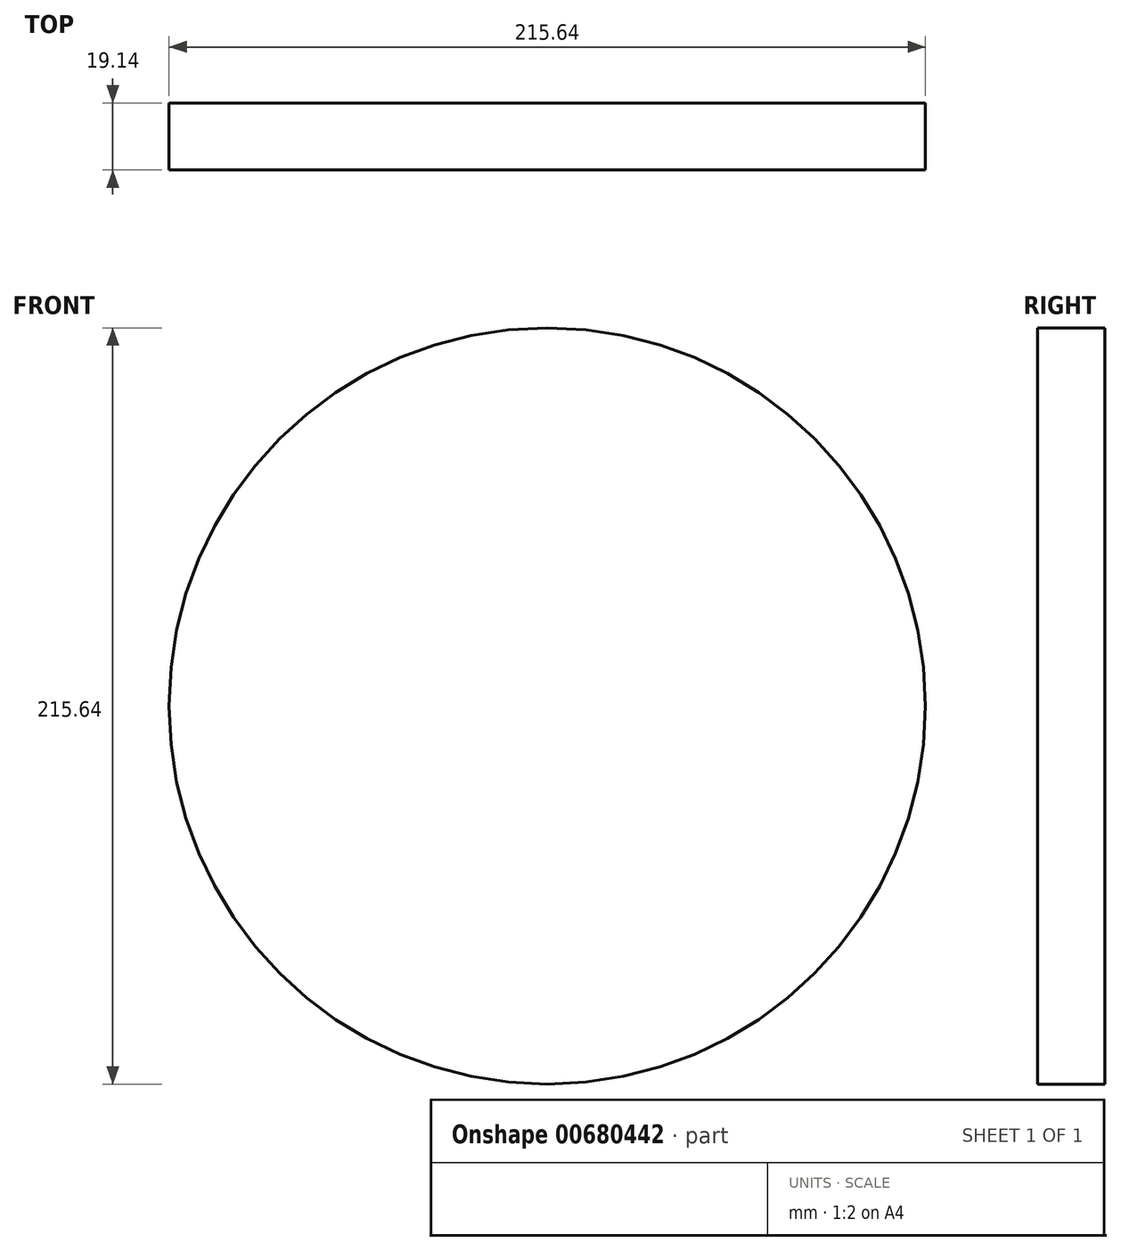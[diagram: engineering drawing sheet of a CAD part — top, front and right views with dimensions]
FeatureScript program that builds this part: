
annotation { "Feature Type Name" : "Feature", "Feature Type Description" : "" }
export const myFeature = defineFeature(function(context is Context, id is Id, definition is map)
    precondition{}
    {
        {
            var Q0;
            Q0=qCreatedBy(makeId("Front.planeOp"),FACE);
            var sketch = newSketch(context, id + "F0", { "sketchPlane" : qUnion([Q0])});
            skCircle(sketch, "E0", {"center": v(0, 0) * mm, "radius": 107.82 * mm});
            skSolve(sketch);
        }
        {
            var Q0;
            Q0=makeQuery(id+"F0.imprint","IMPRINT",FACE,{"disambiguationData":[TD([[makeQuery(id+"F0.imprint","IMPRINT",EDGE,{"derivedFrom":sQuery(id+"F0.wireOp",EDGE,"E0")}),1.0]])]});
            extrude(context, id + "F1", {"entities" : qUnion([Q0]), "depth" : 19.14 * mm, "offsetDistance" : 25.4 * mm});
        }
    });
